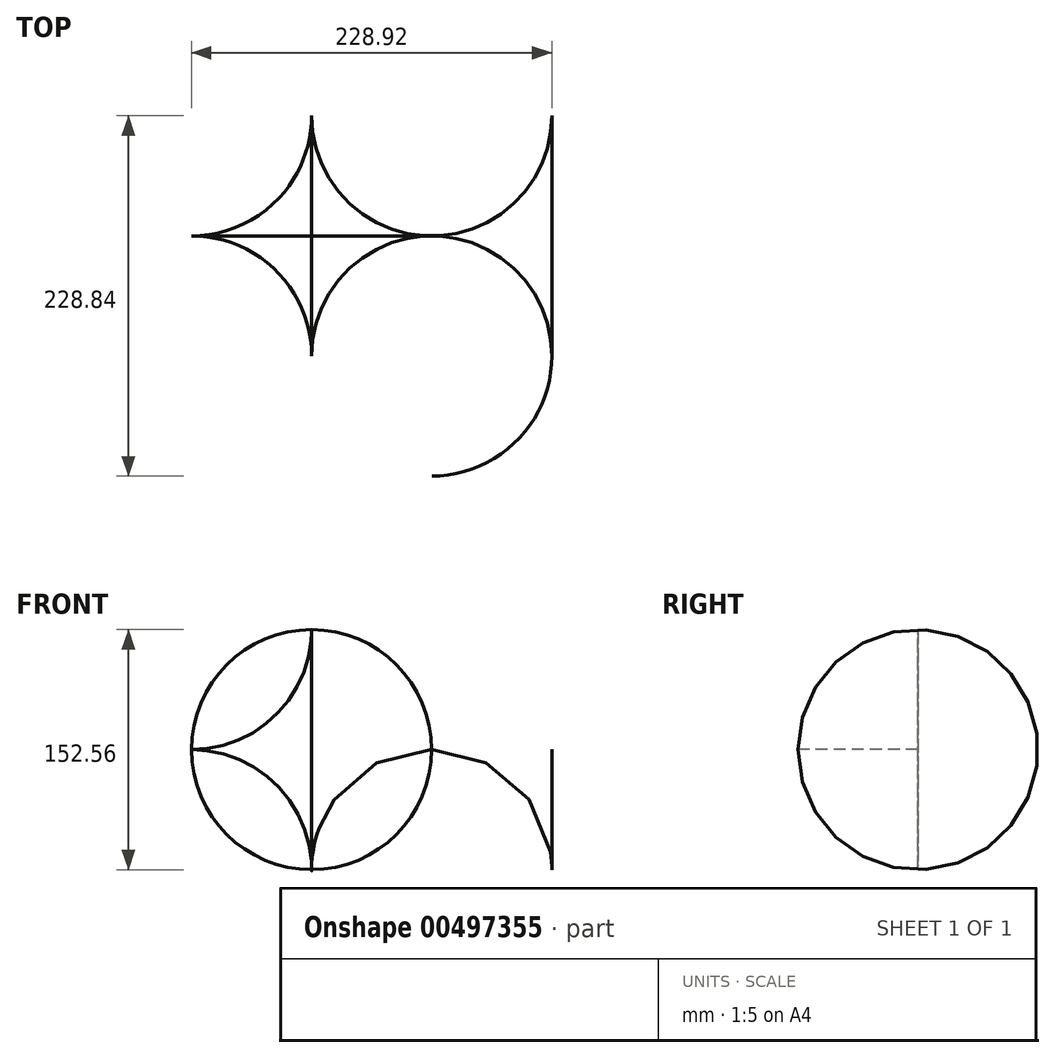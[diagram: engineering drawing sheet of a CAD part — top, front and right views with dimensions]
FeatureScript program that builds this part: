
annotation { "Feature Type Name" : "Feature", "Feature Type Description" : "" }
export const myFeature = defineFeature(function(context is Context, id is Id, definition is map)
    precondition{}
    {
        {
            var Q0;
            Q0=qCreatedBy(makeId("Top.planeOp"),FACE);
            var sketch = newSketch(context, id + "F0", { "sketchPlane" : qUnion([Q0])});
            skPoint(sketch, "E0.endSnap0", {"position": v(0, 63.6) * mm});
            skPoint(sketch, "E1.endSnap0", {"position": v(-25.4, 0) * mm});
            skLineSegment(sketch, "E2", {"start": v(-76.2, 0) * mm, "end": v(76.2, 0) * mm});
            skLineSegment(sketch, "E3", {"start": v(0, 76.28) * mm, "end": v(0, 0) * mm});
            skArc(sketch, "E4", {"start": v(0, 76.28) * mm, "mid": v(22.31, 22.37) * mm, "end": v(76.2, 0) * mm});
            skArc(sketch, "E5", {"start": v(-76.2, 0) * mm, "mid": v(-22.31, 22.37) * mm, "end": v(0, 76.28) * mm});
            skSolve(sketch);
        }
        {
            var Q0;
            Q0=qCreatedBy(makeId("Top.planeOp"),FACE);
            var sketch = newSketch(context, id + "F1", { "sketchPlane" : qUnion([Q0])});
            skLineSegment(sketch, "E6", {"start": v(0, 0) * mm, "end": v(0, 76.2) * mm});
            skArc(sketch, "E7", {"start": v(-76.2, 0) * mm, "mid": v(-22.32, 22.32) * mm, "end": v(0, 76.2) * mm});
            skArc(sketch, "E8", {"start": v(0, -76.2) * mm, "mid": v(-22.32, -22.32) * mm, "end": v(-76.2, 0) * mm});
            skLineSegment(sketch, "E9", {"start": v(0, 76.2) * mm, "end": v(0, -76.2) * mm});
            skLineSegment(sketch, "E10", {"start": v(-76.2, 0) * mm, "end": v(0, 0) * mm});
            skSolve(sketch);
        }
        {
            var Q0;
            Q0=qCreatedBy(makeId("Right.planeOp"),FACE);
            var sketch = newSketch(context, id + "F2", { "sketchPlane" : qUnion([Q0])});
            skArc(sketch, "E11", {"start": v(-76.2, 0) * mm, "mid": v(-22.32, 22.32) * mm, "end": v(0, 76.2) * mm});
            skArc(sketch, "E12", {"start": v(0, 76.2) * mm, "mid": v(22.32, 22.32) * mm, "end": v(76.2, 0) * mm});
            skLineSegment(sketch, "E13", {"start": v(-76.2, 0) * mm, "end": v(76.2, 0) * mm});
            skSolve(sketch);
        }
        {
            var Q0;
            Q0 = qSketchRegion(id + "F0", true);
            var Q1;
            Q1=sQuery(id+"F0.wireOp",EDGE,"E2");
            revolve(context, id + "F3", {"entities" : qUnion([Q0]), "axis" : qUnion([Q1]), "revolveType" : RevolveType.FULL});
        }
        {
            var Q0;
            Q0 = qSketchRegion(id + "F1", true);
            var Q1;
            Q1=sQuery(id+"F1.wireOp",EDGE,"E9");
            revolve(context, id + "F4", {"entities" : qUnion([Q0]), "axis" : qUnion([Q1]), "revolveType" : RevolveType.FULL});
        }
        {
            var Q0;
            Q0 = qSketchRegion(id + "F2", true);
            var Q1;
            Q1=sQuery(id+"F2.wireOp",EDGE,"E13");
            revolve(context, id + "F5", {"entities" : qUnion([Q0]), "axis" : qUnion([Q1]), "revolveType" : RevolveType.FULL});
        }
    });
